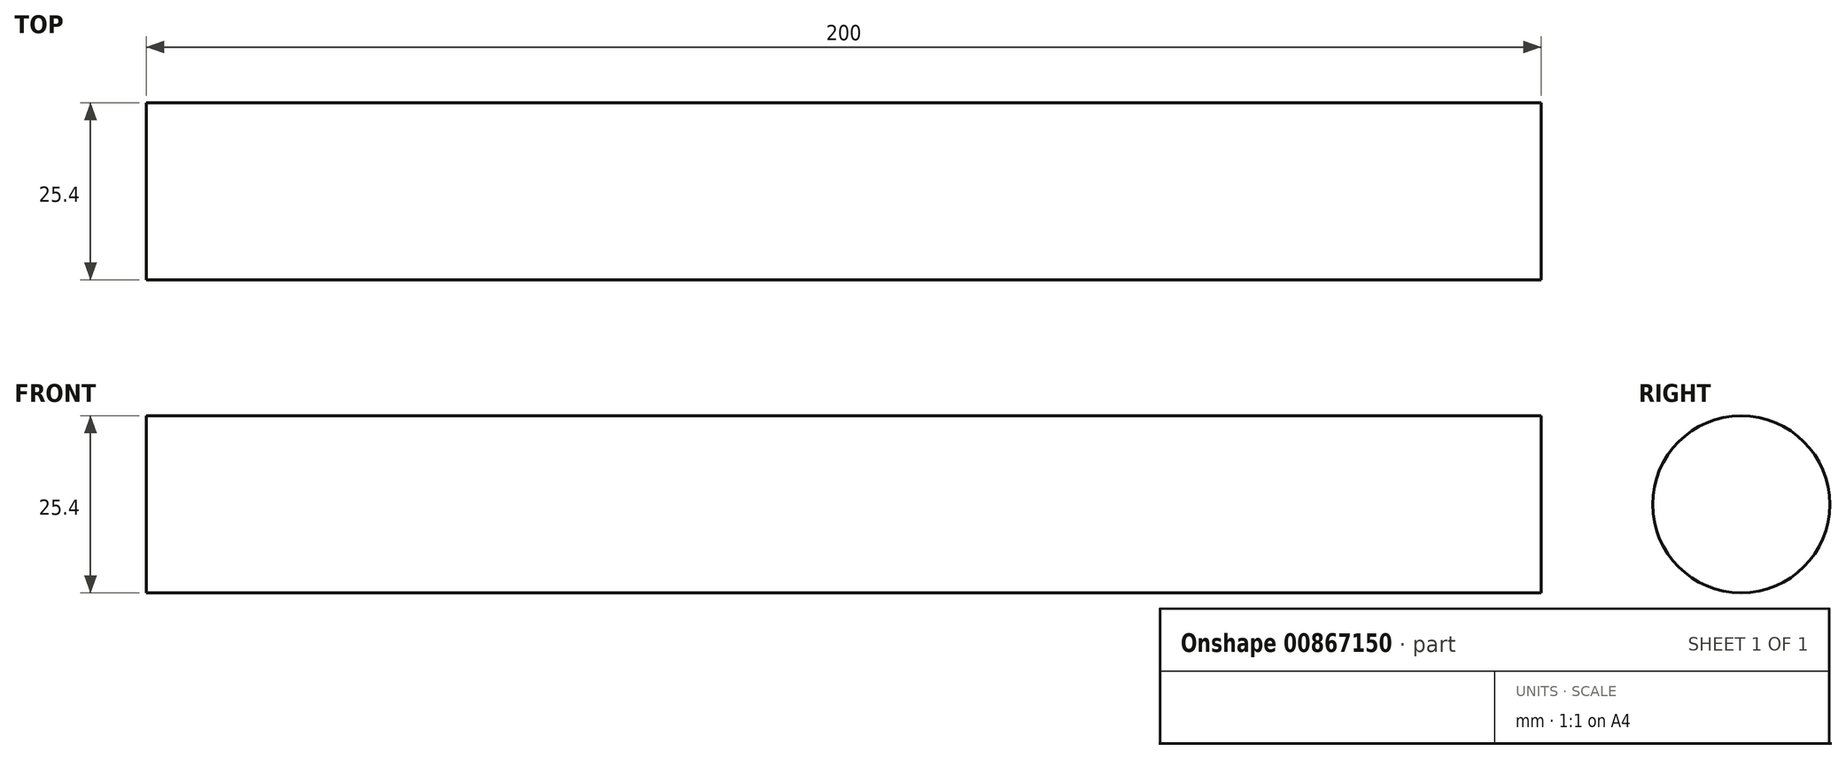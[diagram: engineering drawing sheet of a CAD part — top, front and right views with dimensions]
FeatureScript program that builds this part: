
annotation { "Feature Type Name" : "Feature", "Feature Type Description" : "" }
export const myFeature = defineFeature(function(context is Context, id is Id, definition is map)
    precondition{}
    {
        {
            var Q0;
            Q0=qCreatedBy(makeId("Right.planeOp"),FACE);
            var sketch = newSketch(context, id + "F0", { "sketchPlane" : qUnion([Q0])});
            skCircle(sketch, "E0", {"center": v(0, 0) * mm, "radius": 12.7 * mm});
            skSolve(sketch);
        }
        {
            var Q0;
            Q0=qSketchRegion(id+"F0",true);
            extrude(context, id + "F1", {"entities" : qUnion([Q0]), "depth" : 200 * mm, "offsetDistance" : 25 * mm});
        }
    });
